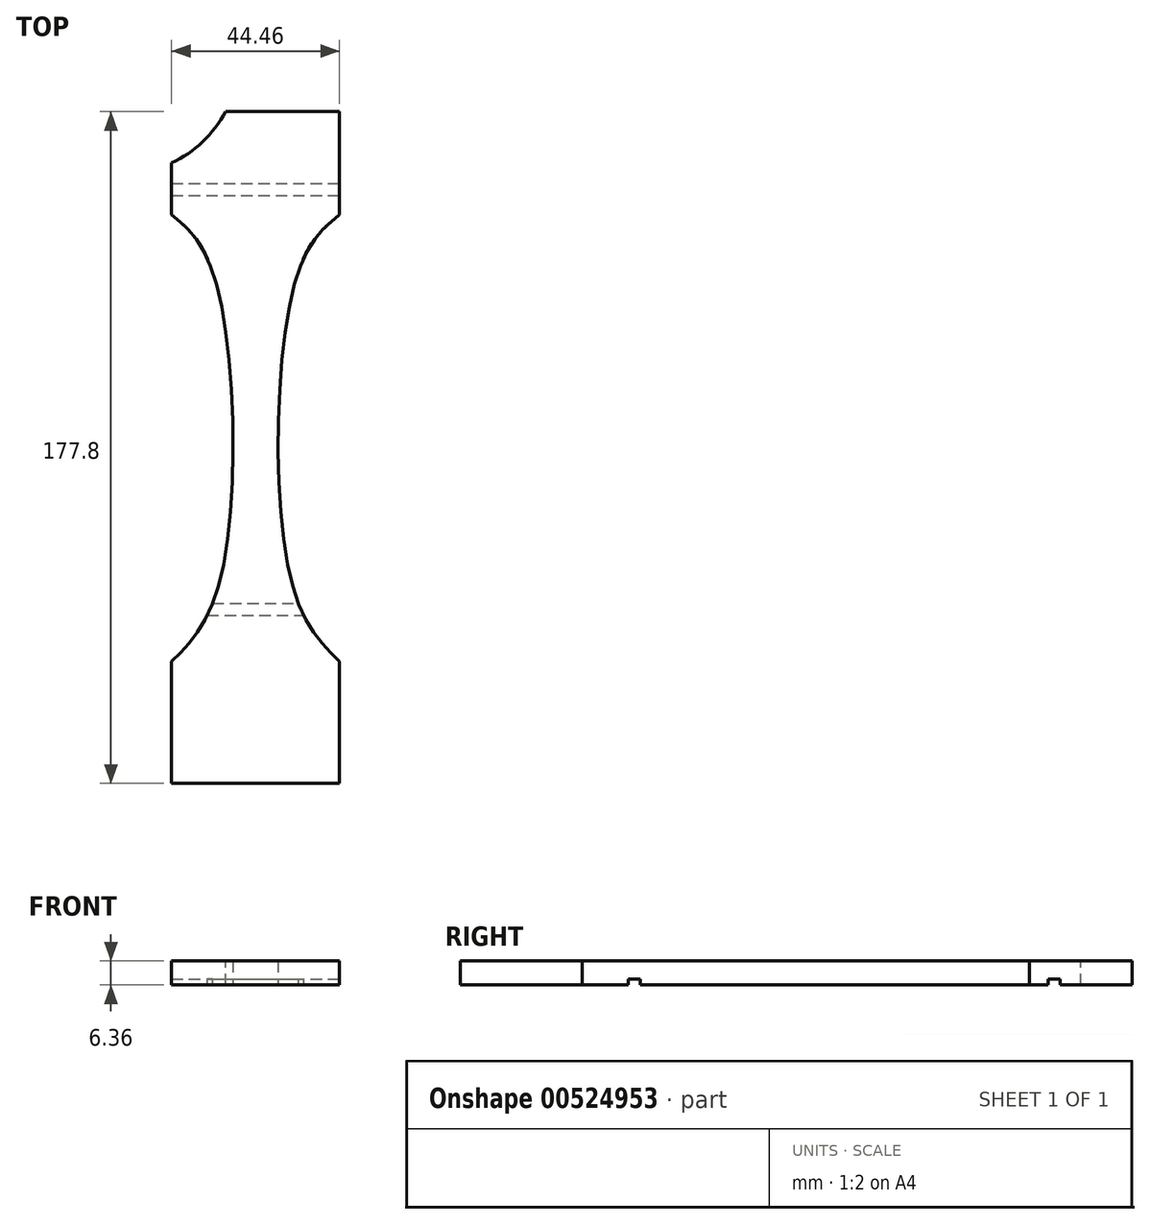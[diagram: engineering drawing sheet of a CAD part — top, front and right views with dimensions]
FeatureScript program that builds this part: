
annotation { "Feature Type Name" : "Feature", "Feature Type Description" : "" }
export const myFeature = defineFeature(function(context is Context, id is Id, definition is map)
    precondition{}
    {
        {
            var Q0;
            Q0=qCreatedBy(makeId("Front.planeOp"),FACE);
            var sketch = newSketch(context, id + "F0", { "sketchPlane" : qUnion([Q0])});
            skLineSegment(sketch, "E0.bottom", {"start": v(22.22, 15.88) * mm, "end": v(-22.23, 15.88) * mm});
            skLineSegment(sketch, "E0.top", {"start": v(22.23, -15.88) * mm, "end": v(-22.22, -15.88) * mm});
            skLineSegment(sketch, "E0.left", {"start": v(22.22, 15.88) * mm, "end": v(22.23, -15.88) * mm});
            skLineSegment(sketch, "E0.right", {"start": v(-22.23, 15.88) * mm, "end": v(-22.22, -15.88) * mm});
            skPoint(sketch, "E0.middle", {"position": v(0, 0) * mm});
            skSolve(sketch);
        }
        {
            var Q0;
            Q0=makeQuery(id+"F0.imprint","IMPRINT",FACE,{"disambiguationData":[TD([[makeQuery(id+"F0.imprint","IMPRINT",EDGE,{"derivedFrom":sQuery(id+"F0.wireOp",EDGE,"E0.bottom")}),1.0]])]});
            extrude(context, id + "F1", {"entities" : qUnion([Q0]), "oppositeDirection" : true, "depth" : 177.8 * mm});
        }
        {
            var Q0;
            Q0=makeQuery(id+"F1.opExtrude","SWEPT_FACE",FACE,{"disambiguationData":[OSD([sQuery(id+"F0.wireOp",EDGE,"E0.left")])]});
            var sketch = newSketch(context, id + "F2", { "sketchPlane" : qUnion([Q0])});
            skLineSegment(sketch, "E1.bottom", {"start": v(44.45, -15.88) * mm, "end": v(47.62, -15.88) * mm});
            skLineSegment(sketch, "E2.bottom", {"start": v(155.57, -15.88) * mm, "end": v(158.75, -15.88) * mm});
            skArc(sketch, "E3", {"start": v(47.62, -15.88) * mm, "mid": v(46.04, -14.29) * mm, "end": v(44.45, -15.88) * mm});
            skArc(sketch, "E4", {"start": v(158.75, -15.88) * mm, "mid": v(157.16, -14.29) * mm, "end": v(155.57, -15.88) * mm});
            skPoint(sketch, "E5.oppositeSnap0", {"position": v(46.04, -14.29) * mm});
            skLineSegment(sketch, "E5.top", {"start": v(44.45, -14.29) * mm, "end": v(47.62, -14.29) * mm});
            skLineSegment(sketch, "E5.left", {"start": v(44.45, -15.88) * mm, "end": v(44.45, -14.29) * mm});
            skLineSegment(sketch, "E5.right", {"start": v(47.62, -15.88) * mm, "end": v(47.62, -14.29) * mm});
            skLineSegment(sketch, "E6.top", {"start": v(155.58, -14.29) * mm, "end": v(158.75, -14.29) * mm});
            skLineSegment(sketch, "E6.left", {"start": v(155.57, -15.88) * mm, "end": v(155.57, -14.29) * mm});
            skLineSegment(sketch, "E6.right", {"start": v(158.75, -15.88) * mm, "end": v(158.75, -14.29) * mm});
            skSolve(sketch);
        }
        {
            var Q0;
            {var subQ0=sQuery(id+"F2.wireOp",EDGE,"E1.bottom");Q0=makeQuery(id+"F2.imprint","IMPRINT",FACE,{"disambiguationData":[TD([[makeQuery(id+"F2.imprint","IMPRINT",EDGE,{"derivedFrom":subQ0}),-1.0]])]});}
            var Q1;
            {var subQ0=sQuery(id+"F2.wireOp",EDGE,"E5.right");Q1=makeQuery(id+"F2.imprint","IMPRINT",FACE,{"disambiguationData":[TD([[makeQuery(id+"F2.imprint","IMPRINT",EDGE,{"derivedFrom":subQ0}),1.0]])]});}
            var Q2;
            {var subQ0=sQuery(id+"F2.wireOp",EDGE,"E5.left");Q2=makeQuery(id+"F2.imprint","IMPRINT",FACE,{"disambiguationData":[TD([[makeQuery(id+"F2.imprint","IMPRINT",EDGE,{"derivedFrom":subQ0}),-1.0]])]});}
            var Q3;
            {var subQ0=sQuery(id+"F2.wireOp",EDGE,"E2.bottom");Q3=makeQuery(id+"F2.imprint","IMPRINT",FACE,{"disambiguationData":[TD([[makeQuery(id+"F2.imprint","IMPRINT",EDGE,{"derivedFrom":subQ0}),-1.0]])]});}
            var Q4;
            {var subQ0=sQuery(id+"F2.wireOp",EDGE,"E6.right");Q4=makeQuery(id+"F2.imprint","IMPRINT",FACE,{"disambiguationData":[TD([[makeQuery(id+"F2.imprint","IMPRINT",EDGE,{"derivedFrom":subQ0}),1.0]])]});}
            var Q5;
            {var subQ0=sQuery(id+"F2.wireOp",EDGE,"E6.left");Q5=makeQuery(id+"F2.imprint","IMPRINT",FACE,{"disambiguationData":[TD([[makeQuery(id+"F2.imprint","IMPRINT",EDGE,{"derivedFrom":subQ0}),-1.0]])]});}
            extrude(context, id + "F3", {"entities" : qUnion([Q0, Q1, Q2, Q3, Q4, Q5]), "operationType" : NewBodyOperationType.REMOVE, "endBound" : BoundingType.THROUGH_ALL, "oppositeDirection" : true, "depth" : 25.4 * mm});
        }
        {
            var Q0;
            Q0=makeQuery(id+"F1.opExtrude","SWEPT_FACE",FACE,{"disambiguationData":[OSD([sQuery(id+"F0.wireOp",EDGE,"E0.left")])]});
            var sketch = newSketch(context, id + "F4", { "sketchPlane" : qUnion([Q0])});
            skLineSegment(sketch, "E7", {"start": v(177.8, -9.52) * mm, "end": v(0, -9.52) * mm});
            skLineSegment(sketch, "E8.bottom", {"start": v(177.8, 15.88) * mm, "end": v(0, 15.88) * mm});
            skLineSegment(sketch, "E8.left", {"start": v(177.8, 15.88) * mm, "end": v(177.8, -9.52) * mm});
            skLineSegment(sketch, "E8.right", {"start": v(0, 15.88) * mm, "end": v(0, -9.52) * mm});
            skSolve(sketch);
        }
        {
            var Q0;
            Q0=makeQuery(id+"F4.imprint","IMPRINT",FACE,{"disambiguationData":[TD([[makeQuery(id+"F4.imprint","IMPRINT",EDGE,{"derivedFrom":sQuery(id+"F4.wireOp",EDGE,"E8.bottom")}),1.0]])]});
            extrude(context, id + "F5", {"entities" : qUnion([Q0]), "operationType" : NewBodyOperationType.REMOVE, "oppositeDirection" : true, "depth" : 66.04 * mm, "offsetDistance" : 25.4 * mm});
        }
        {
            var Q0;
            Q0=makeQuery(id+"F5.boolean.opBoolean","COPY",FACE,{"derivedFrom":makeQuery(id+"F5.opExtrude","SWEPT_FACE",FACE,{"disambiguationData":[OSD([sQuery(id+"F4.wireOp",EDGE,"E7")])]})});
            var sketch = newSketch(context, id + "F6", { "sketchPlane" : qUnion([Q0])});
            skFitSpline(sketch, "E9", {"points": [v(-22.23, 150.56) * mm, v(-11.03, 134.52) * mm, v(-9.52, 53.3) * mm, v(-22.23, 32.25) * mm], "startDerivative": vector(51.6, -43.22) * mm, "endDerivative": vector(-54.2, -54.05) * mm});
            skFitSpline(sketch, "E10.MirrorCS", {"points": [v(22.22, 150.56) * mm, v(11.03, 134.52) * mm, v(9.52, 53.3) * mm, v(22.22, 32.25) * mm], "startDerivative": vector(-51.6, -43.22) * mm, "endDerivative": vector(54.2, -54.05) * mm});
            skSolve(sketch);
        }
        {
            var Q0;
            {var subQ0=sQuery(id+"F6.wireOp",EDGE,"E9");Q0=makeQuery(id+"F6.imprint","IMPRINT",FACE,{"disambiguationData":[TD([[makeQuery(id+"F6.imprint","IMPRINT",EDGE,{"derivedFrom":subQ0}),-1.0]])]});}
            var Q1;
            {var subQ0=sQuery(id+"F6.wireOp",EDGE,"E10.MirrorCS");Q1=makeQuery(id+"F6.imprint","IMPRINT",FACE,{"disambiguationData":[TD([[makeQuery(id+"F6.imprint","IMPRINT",EDGE,{"derivedFrom":subQ0}),1.0]])]});}
            extrude(context, id + "F7", {"entities" : qUnion([Q0, Q1]), "operationType" : NewBodyOperationType.REMOVE, "oppositeDirection" : true, "depth" : 25.4 * mm, "offsetDistance" : 25.4 * mm});
        }
        {
            var Q0;
            Q0=makeQuery(id+"F5.boolean.opBoolean","COPY",FACE,{"derivedFrom":makeQuery(id+"F5.opExtrude","SWEPT_FACE",FACE,{"disambiguationData":[OSD([sQuery(id+"F4.wireOp",EDGE,"E7")])]})});
            var sketch = newSketch(context, id + "F8", { "sketchPlane" : qUnion([Q0])});
            skArc(sketch, "E11", {"start": v(-22.23, 164.18) * mm, "mid": v(-13.97, 169.83) * mm, "end": v(-7.93, 177.8) * mm});
            skLineSegment(sketch, "E12", {"start": v(0, 177.8) * mm, "end": v(0, 140.47) * mm});
            skLineSegment(sketch, "E13", {"start": v(-7.93, 177.8) * mm, "end": v(-22.23, 177.8) * mm});
            skLineSegment(sketch, "E14", {"start": v(-22.23, 177.8) * mm, "end": v(-22.23, 164.18) * mm});
            skSolve(sketch);
        }
        {
            var Q0;
            Q0=makeQuery(id+"F8.imprint","IMPRINT",FACE,{"disambiguationData":[TD([[makeQuery(id+"F8.imprint","IMPRINT",EDGE,{"derivedFrom":sQuery(id+"F8.wireOp",EDGE,"E11")}),1.0]])]});
            extrude(context, id + "F9", {"entities" : qUnion([Q0]), "operationType" : NewBodyOperationType.REMOVE, "oppositeDirection" : true, "depth" : 25.4 * mm, "offsetDistance" : 25.4 * mm});
        }
    });
